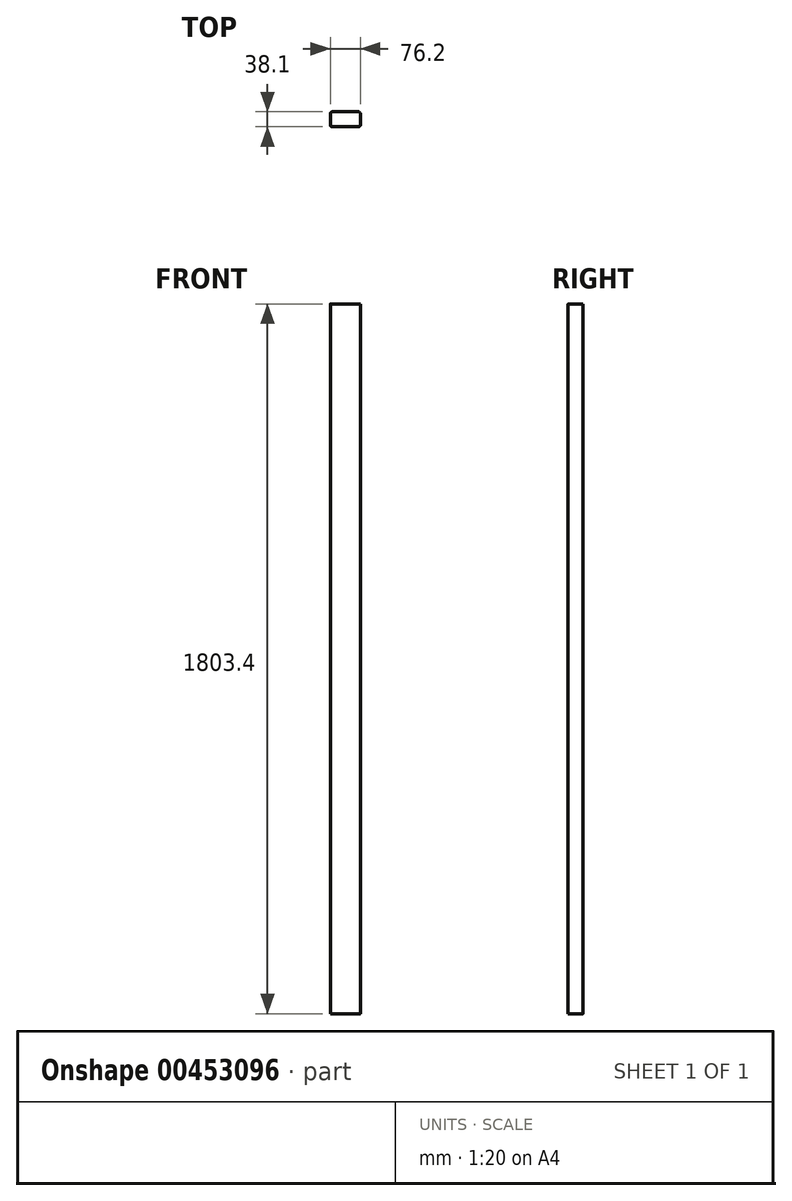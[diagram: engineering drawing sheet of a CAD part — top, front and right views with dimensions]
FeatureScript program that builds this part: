
annotation { "Feature Type Name" : "Feature", "Feature Type Description" : "" }
export const myFeature = defineFeature(function(context is Context, id is Id, definition is map)
    precondition{}
    {
        {
            var Q0;
            Q0=qCreatedBy(makeId("Top.planeOp"),FACE);
            var sketch = newSketch(context, id + "F0", { "sketchPlane" : qUnion([Q0])});
            skLineSegment(sketch, "E0.bottom", {"start": v(38.1, 19.05) * mm, "end": v(-38.1, 19.05) * mm});
            skLineSegment(sketch, "E0.top", {"start": v(38.1, -19.05) * mm, "end": v(-38.1, -19.05) * mm});
            skLineSegment(sketch, "E0.left", {"start": v(38.1, 19.05) * mm, "end": v(38.1, -19.05) * mm});
            skLineSegment(sketch, "E0.right", {"start": v(-38.1, 19.05) * mm, "end": v(-38.1, -19.05) * mm});
            skPoint(sketch, "E0.middle", {"position": v(0, 0) * mm});
            skSolve(sketch);
        }
        {
            var Q0;
            Q0 = qSketchRegion(id + "F0", true);
            extrude(context, id + "F1", {"entities" : qUnion([Q0]), "offsetDistance" : 25.4 * mm, "depth" : 1803.4 * mm});
        }
        {
            var Q0;
            Q0=makeQuery(id+"F1.opExtrude","SWEPT_EDGE",EDGE,{"disambiguationData":[OSD([sQuery(id+"F0.wireOp",EDGE,"E0.top"),sQuery(id+"F0.wireOp",EDGE,"E0.left")])]});
            var Q1;
            Q1=makeQuery(id+"F1.opExtrude","SWEPT_EDGE",EDGE,{"disambiguationData":[OSD([sQuery(id+"F0.wireOp",EDGE,"E0.top"),sQuery(id+"F0.wireOp",EDGE,"E0.right")])]});
            var Q2;
            Q2=makeQuery(id+"F1.opExtrude","SWEPT_EDGE",EDGE,{"disambiguationData":[OSD([sQuery(id+"F0.wireOp",EDGE,"E0.bottom"),sQuery(id+"F0.wireOp",EDGE,"E0.left")])]});
            var Q3;
            Q3=makeQuery(id+"F1.opExtrude","SWEPT_EDGE",EDGE,{"disambiguationData":[OSD([sQuery(id+"F0.wireOp",EDGE,"E0.bottom"),sQuery(id+"F0.wireOp",EDGE,"E0.right")])]});
            fillet(context, id + "F2", {"entities" : qUnion([Q0, Q1, Q2, Q3]), "radius" : 5.08 * mm, "tangentPropagation" : true, "allowEdgeOverflow" : false});
        }
    });
